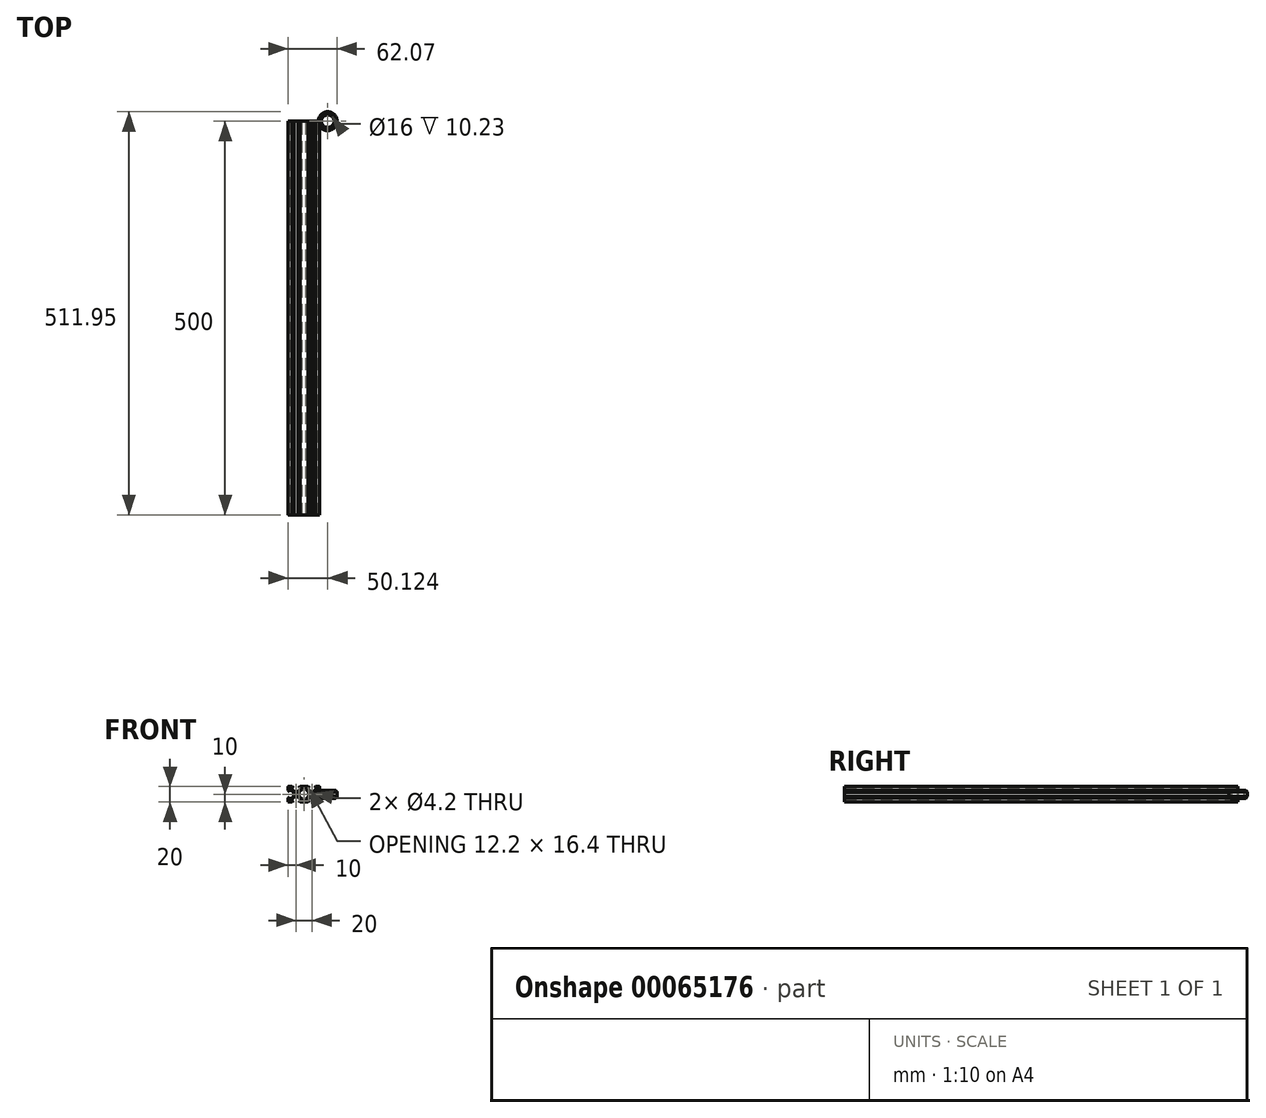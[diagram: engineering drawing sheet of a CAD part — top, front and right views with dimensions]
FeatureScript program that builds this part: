
annotation { "Feature Type Name" : "Feature", "Feature Type Description" : "" }
export const myFeature = defineFeature(function(context is Context, id is Id, definition is map)
    precondition{}
    {
        {
            var Q0;
            Q0=qCreatedBy(makeId("Front.planeOp"),FACE);
            var sketch = newSketch(context, id + "F0", { "sketchPlane" : qUnion([Q0])});
            skLineSegment(sketch, "E0", {"start": v(2.7, -8.2) * mm, "end": v(2.7, -6.24) * mm});
            skLineSegment(sketch, "E1", {"start": v(2.7, -6.24) * mm, "end": v(6.1, -2.84) * mm});
            skLineSegment(sketch, "E2", {"start": v(6.1, -2.84) * mm, "end": v(6.1, 2.84) * mm});
            skLineSegment(sketch, "E3", {"start": v(6.1, 2.84) * mm, "end": v(2.7, 6.24) * mm});
            skLineSegment(sketch, "E4", {"start": v(2.7, 6.24) * mm, "end": v(2.7, 8.2) * mm});
            skLineSegment(sketch, "E5", {"start": v(2.7, 8.2) * mm, "end": v(0, 8.2) * mm});
            skLineSegment(sketch, "E6", {"start": v(0, 8.2) * mm, "end": v(0, 0) * mm});
            skLineSegment(sketch, "E7", {"start": v(2.7, -8.2) * mm, "end": v(0, -8.2) * mm});
            skLineSegment(sketch, "E8", {"start": v(0, -8.2) * mm, "end": v(0, 0) * mm});
            skPoint(sketch, "E9.middle", {"position": v(0, 0) * mm});
            skLineSegment(sketch, "E10", {"start": v(5.07, 10) * mm, "end": v(0, 10) * mm});
            skLineSegment(sketch, "E11", {"start": v(0, 10) * mm, "end": v(0, 8.2) * mm});
            skLineSegment(sketch, "E12", {"start": v(0, -10) * mm, "end": v(0, -8.2) * mm});
            skPoint(sketch, "E13.endSnap0", {"position": v(6.1, 0) * mm});
            skLineSegment(sketch, "E14", {"start": v(0, -10) * mm, "end": v(5.07, -10) * mm});
            skCircle(sketch, "E15", {"center": v(10, 0) * mm, "radius": 2.1 * mm});
            skLineSegment(sketch, "E16", {"start": v(5.07, 10) * mm, "end": v(6.87, 8.2) * mm});
            skLineSegment(sketch, "E17", {"start": v(6.87, 8.2) * mm, "end": v(4.5, 8.2) * mm});
            skLineSegment(sketch, "E18", {"start": v(4.5, 8.2) * mm, "end": v(4.5, 6.56) * mm});
            skLineSegment(sketch, "E19", {"start": v(4.5, 6.56) * mm, "end": v(7.53, 3.53) * mm});
            skPoint(sketch, "E20.endSnap0", {"position": v(9.63, 5.16) * mm});
            skLineSegment(sketch, "E21", {"start": v(7.53, 3.53) * mm, "end": v(10, 3.53) * mm});
            skLineSegment(sketch, "E22.MirrorCS", {"start": v(12.47, 3.53) * mm, "end": v(10, 3.53) * mm});
            skLineSegment(sketch, "E23.MirrorCS", {"start": v(15.5, 6.56) * mm, "end": v(12.47, 3.53) * mm});
            skLineSegment(sketch, "E24.MirrorCS", {"start": v(15.5, 8.2) * mm, "end": v(15.5, 6.56) * mm});
            skLineSegment(sketch, "E25.MirrorCS", {"start": v(13.13, 8.2) * mm, "end": v(15.5, 8.2) * mm});
            skLineSegment(sketch, "E26.MirrorCS", {"start": v(14.93, 10) * mm, "end": v(13.13, 8.2) * mm});
            skLineSegment(sketch, "E27.MirrorCS", {"start": v(14.93, 10) * mm, "end": v(19.5, 10) * mm});
            skLineSegment(sketch, "E28.MirrorCS", {"start": v(20, 4.93) * mm, "end": v(18.2, 3.12) * mm});
            skLineSegment(sketch, "E29.MirrorCS", {"start": v(18.2, 5.5) * mm, "end": v(16.56, 5.5) * mm});
            skLineSegment(sketch, "E30.MirrorCS", {"start": v(16.56, 5.5) * mm, "end": v(13.53, 2.47) * mm});
            skLineSegment(sketch, "E31.MirrorCS", {"start": v(13.53, -2.47) * mm, "end": v(13.53, 0) * mm});
            skLineSegment(sketch, "E32.MirrorCS", {"start": v(13.53, 2.47) * mm, "end": v(13.53, 0) * mm});
            skLineSegment(sketch, "E33.MirrorCS", {"start": v(18.2, 3.12) * mm, "end": v(18.2, 5.5) * mm});
            skLineSegment(sketch, "E34.MirrorCS", {"start": v(16.56, -5.5) * mm, "end": v(13.53, -2.47) * mm});
            skLineSegment(sketch, "E35.MirrorCS", {"start": v(18.2, -5.5) * mm, "end": v(16.56, -5.5) * mm});
            skLineSegment(sketch, "E36.MirrorCS", {"start": v(18.2, -3.13) * mm, "end": v(18.2, -5.5) * mm});
            skLineSegment(sketch, "E37.MirrorCS", {"start": v(20, -4.93) * mm, "end": v(18.2, -3.12) * mm});
            skLineSegment(sketch, "E38", {"start": v(20, 9.5) * mm, "end": v(20, 4.93) * mm});
            skLineSegment(sketch, "E39.MirrorCS", {"start": v(20, -9.5) * mm, "end": v(20, -4.93) * mm});
            skLineSegment(sketch, "E40.MirrorCS", {"start": v(14.93, -10) * mm, "end": v(19.5, -10) * mm});
            skLineSegment(sketch, "E41.MirrorCS", {"start": v(14.93, -10) * mm, "end": v(13.13, -8.2) * mm});
            skLineSegment(sketch, "E42.MirrorCS", {"start": v(13.13, -8.2) * mm, "end": v(15.5, -8.2) * mm});
            skLineSegment(sketch, "E43.MirrorCS", {"start": v(15.5, -8.2) * mm, "end": v(15.5, -6.56) * mm});
            skLineSegment(sketch, "E44.MirrorCS", {"start": v(15.5, -6.56) * mm, "end": v(12.47, -3.53) * mm});
            skLineSegment(sketch, "E45.MirrorCS", {"start": v(12.47, -3.53) * mm, "end": v(10, -3.53) * mm});
            skLineSegment(sketch, "E46.MirrorCS", {"start": v(7.53, -3.53) * mm, "end": v(10, -3.53) * mm});
            skLineSegment(sketch, "E47.MirrorCS", {"start": v(4.5, -6.56) * mm, "end": v(7.53, -3.53) * mm});
            skLineSegment(sketch, "E48.MirrorCS", {"start": v(4.5, -8.2) * mm, "end": v(4.5, -6.56) * mm});
            skLineSegment(sketch, "E49.MirrorCS", {"start": v(6.87, -8.2) * mm, "end": v(4.5, -8.2) * mm});
            skLineSegment(sketch, "E50.MirrorCS", {"start": v(5.07, -10) * mm, "end": v(6.87, -8.2) * mm});
            skLineSegment(sketch, "E51.MirrorCS", {"start": v(-7.53, 3.53) * mm, "end": v(-10, 3.53) * mm});
            skCircle(sketch, "E52.MirrorC", {"center": v(-10, 0) * mm, "radius": 2.1 * mm});
            skLineSegment(sketch, "E53.MirrorCS", {"start": v(-6.1, -2.84) * mm, "end": v(-6.1, 2.84) * mm});
            skLineSegment(sketch, "E54.MirrorCS", {"start": v(-18.2, -3.13) * mm, "end": v(-18.2, -5.5) * mm});
            skLineSegment(sketch, "E55.MirrorCS", {"start": v(-14.93, 10) * mm, "end": v(-19.5, 10) * mm});
            skLineSegment(sketch, "E56.MirrorCS", {"start": v(0, -10) * mm, "end": v(-5.07, -10) * mm});
            skLineSegment(sketch, "E57.MirrorCS", {"start": v(-14.93, -10) * mm, "end": v(-13.13, -8.2) * mm});
            skLineSegment(sketch, "E58.MirrorCS", {"start": v(-14.93, 10) * mm, "end": v(-13.13, 8.2) * mm});
            skLineSegment(sketch, "E59.MirrorCS", {"start": v(-6.87, 8.2) * mm, "end": v(-4.5, 8.2) * mm});
            skLineSegment(sketch, "E60.MirrorCS", {"start": v(-20, -4.93) * mm, "end": v(-18.2, -3.12) * mm});
            skLineSegment(sketch, "E61.MirrorCS", {"start": v(-2.7, -8.2) * mm, "end": v(0, -8.2) * mm});
            skLineSegment(sketch, "E62.MirrorCS", {"start": v(-20, 4.93) * mm, "end": v(-18.2, 3.12) * mm});
            skLineSegment(sketch, "E63.MirrorCS", {"start": v(-2.7, -8.2) * mm, "end": v(-2.7, -6.24) * mm});
            skLineSegment(sketch, "E64.MirrorCS", {"start": v(-7.53, -3.53) * mm, "end": v(-10, -3.53) * mm});
            skLineSegment(sketch, "E65.MirrorCS", {"start": v(-13.13, -8.2) * mm, "end": v(-15.5, -8.2) * mm});
            skLineSegment(sketch, "E66.MirrorCS", {"start": v(-14.93, -10) * mm, "end": v(-19.5, -10) * mm});
            skLineSegment(sketch, "E67.MirrorCS", {"start": v(-6.87, -8.2) * mm, "end": v(-4.5, -8.2) * mm});
            skLineSegment(sketch, "E68.MirrorCS", {"start": v(-5.07, 10) * mm, "end": v(-6.87, 8.2) * mm});
            skLineSegment(sketch, "E69.MirrorCS", {"start": v(-13.53, 2.47) * mm, "end": v(-13.53, 0) * mm});
            skPoint(sketch, "E70.MirrorP", {"position": v(-6.1, 0) * mm});
            skLineSegment(sketch, "E71.MirrorCS", {"start": v(-15.5, -8.2) * mm, "end": v(-15.5, -6.56) * mm});
            skLineSegment(sketch, "E72.MirrorCS", {"start": v(-5.07, 10) * mm, "end": v(0, 10) * mm});
            skLineSegment(sketch, "E73.MirrorCS", {"start": v(-20, 9.5) * mm, "end": v(-20, 4.93) * mm});
            skLineSegment(sketch, "E74.MirrorCS", {"start": v(-18.2, 5.5) * mm, "end": v(-16.56, 5.5) * mm});
            skLineSegment(sketch, "E75.MirrorCS", {"start": v(-18.2, 3.12) * mm, "end": v(-18.2, 5.5) * mm});
            skLineSegment(sketch, "E76.MirrorCS", {"start": v(-15.5, 8.2) * mm, "end": v(-15.5, 6.56) * mm});
            skLineSegment(sketch, "E77.MirrorCS", {"start": v(-2.7, 6.24) * mm, "end": v(-2.7, 8.2) * mm});
            skLineSegment(sketch, "E78.MirrorCS", {"start": v(-16.56, 5.5) * mm, "end": v(-13.53, 2.47) * mm});
            skLineSegment(sketch, "E79.MirrorCS", {"start": v(-15.5, 6.56) * mm, "end": v(-12.47, 3.53) * mm});
            skLineSegment(sketch, "E80.MirrorCS", {"start": v(-16.56, -5.5) * mm, "end": v(-13.53, -2.47) * mm});
            skLineSegment(sketch, "E81.MirrorCS", {"start": v(-4.5, 6.56) * mm, "end": v(-7.53, 3.53) * mm});
            skLineSegment(sketch, "E82.MirrorCS", {"start": v(-20, -9.5) * mm, "end": v(-20, -4.93) * mm});
            skLineSegment(sketch, "E83.MirrorCS", {"start": v(-2.7, -6.24) * mm, "end": v(-6.1, -2.84) * mm});
            skLineSegment(sketch, "E84.MirrorCS", {"start": v(-4.5, 8.2) * mm, "end": v(-4.5, 6.56) * mm});
            skLineSegment(sketch, "E85.MirrorCS", {"start": v(-18.2, -5.5) * mm, "end": v(-16.56, -5.5) * mm});
            skLineSegment(sketch, "E86.MirrorCS", {"start": v(-4.5, -8.2) * mm, "end": v(-4.5, -6.56) * mm});
            skLineSegment(sketch, "E87.MirrorCS", {"start": v(-12.47, 3.53) * mm, "end": v(-10, 3.53) * mm});
            skLineSegment(sketch, "E88.MirrorCS", {"start": v(-13.53, -2.47) * mm, "end": v(-13.53, 0) * mm});
            skLineSegment(sketch, "E89.MirrorCS", {"start": v(-6.1, 2.84) * mm, "end": v(-2.7, 6.24) * mm});
            skLineSegment(sketch, "E90.MirrorCS", {"start": v(-15.5, -6.56) * mm, "end": v(-12.47, -3.53) * mm});
            skLineSegment(sketch, "E91.MirrorCS", {"start": v(-2.7, 8.2) * mm, "end": v(0, 8.2) * mm});
            skLineSegment(sketch, "E92.MirrorCS", {"start": v(-5.07, -10) * mm, "end": v(-6.87, -8.2) * mm});
            skLineSegment(sketch, "E93.MirrorCS", {"start": v(-4.5, -6.56) * mm, "end": v(-7.53, -3.53) * mm});
            skLineSegment(sketch, "E94.MirrorCS", {"start": v(-12.47, -3.53) * mm, "end": v(-10, -3.53) * mm});
            skLineSegment(sketch, "E95.MirrorCS", {"start": v(-13.13, 8.2) * mm, "end": v(-15.5, 8.2) * mm});
            skPoint(sketch, "E96.MirrorP", {"position": v(-9.63, 5.16) * mm});
            skPoint(sketch, "E97.visualSharp", {"position": v(20, 10) * mm});
            skArc(sketch, "E97.filletArc", {"start": v(20, 9.5) * mm, "mid": v(19.85, 9.85) * mm, "end": v(19.5, 10) * mm});
            skPoint(sketch, "E98.visualSharp", {"position": v(20, -10) * mm});
            skArc(sketch, "E98.filletArc", {"start": v(19.5, -10) * mm, "mid": v(19.85, -9.85) * mm, "end": v(20, -9.5) * mm});
            skPoint(sketch, "E99.visualSharp", {"position": v(-20, -10) * mm});
            skArc(sketch, "E99.filletArc", {"start": v(-20, -9.5) * mm, "mid": v(-19.85, -9.85) * mm, "end": v(-19.5, -10) * mm});
            skPoint(sketch, "E100.visualSharp", {"position": v(-20, 10) * mm});
            skArc(sketch, "E100.filletArc", {"start": v(-19.5, 10) * mm, "mid": v(-19.85, 9.85) * mm, "end": v(-20, 9.5) * mm});
            skSolve(sketch);
        }
        {
            var Q0;
            Q0=makeQuery(id+"F0.imprint","IMPRINT",FACE,{"disambiguationData":[TD([[makeQuery(id+"F0.imprint","IMPRINT",EDGE,{"derivedFrom":sQuery(id+"F0.wireOp",EDGE,"E0")}),-1.0]])]});
            var Q1;
            Q1=makeQuery(id+"F0.imprint","IMPRINT",FACE,{"disambiguationData":[TD([[makeQuery(id+"F0.imprint","IMPRINT",EDGE,{"derivedFrom":sQuery(id+"F0.wireOp",EDGE,"E11")}),-1.0]])]});
            extrude(context, id + "F1", {"entities" : qUnion([Q0, Q1]), "depth" : 500 * mm});
        }
        {
            var Q0;
            Q0=qCreatedBy(makeId("Front.planeOp"),FACE);
            var sketch = newSketch(context, id + "F2", { "sketchPlane" : qUnion([Q0])});
            skPoint(sketch, "E101.middle", {"position": v(30.12, 0) * mm});
            skPoint(sketch, "E102.endSnap0", {"position": v(42.07, 0) * mm});
            skLineSegment(sketch, "E103", {"start": v(39.9, 5.12) * mm, "end": v(42.07, 2.94) * mm});
            skLineSegment(sketch, "E104.MirrorCS", {"start": v(39.9, -5.12) * mm, "end": v(42.07, -2.94) * mm});
            skLineSegment(sketch, "E105", {"start": v(30.12, 5.12) * mm, "end": v(30.12, -5.12) * mm});
            skLineSegment(sketch, "E106", {"start": v(38.12, 5.12) * mm, "end": v(39.9, 5.12) * mm});
            skLineSegment(sketch, "E107", {"start": v(39.9, -5.12) * mm, "end": v(38.12, -5.12) * mm});
            skLineSegment(sketch, "E108", {"start": v(42.07, 2.94) * mm, "end": v(42.07, -2.94) * mm});
            skLineSegment(sketch, "E109", {"start": v(30.12, -17.22) * mm, "end": v(30.12, 22.33) * mm});
            skLineSegment(sketch, "E110", {"start": v(38.12, 5.12) * mm, "end": v(38.12, -5.12) * mm});
            skLineSegment(sketch, "E111", {"start": v(30.12, 0) * mm, "end": v(0, 0) * mm, "construction": true});
            skSolve(sketch);
        }
        {
            var Q0;
            {var subQ0=sQuery(id+"F2.wireOp",EDGE,"E103");Q0=makeQuery(id+"F2.imprint","IMPRINT",FACE,{"disambiguationData":[TD([[makeQuery(id+"F2.imprint","IMPRINT",EDGE,{"derivedFrom":subQ0}),-1.0]])]});}
            var Q1;
            Q1=sQuery(id+"F2.wireOp",EDGE,"E105");
            revolve(context, id + "F3", {"entities" : qUnion([Q0]), "axis" : qUnion([Q1]), "revolveType" : RevolveType.FULL});
        }
    });
